# Revit family: 306_43d51a85105a496ca2926896a71aef
name_source: partatom
category: Pipe Accessories
units: mm (PartAtom-declared; Revit-internal decimal feet)

## family parameters
Always vertical = Yes
Cut with Voids When Loaded = No
Part Type = Valve - Breaks Into
Round Connector Dimension = Use Diameter
Shared = No
Work Plane-Based = No

## types (8) — shared parameters
CAT0 = Yes
Description = 3-way Control valve VLE132, PN16 external thread
L2D_Min = 3048 mm
MC = No
Manufacturer = ESBE
QmdConnectorList = 301;D;302;D
URL = http://www.esbe.eu
Z4 = 13 mm  [stored 0.0426509 ft]
Z5 = 4 mm  [stored 0.0131234 ft]
Z6 = 2 mm  [stored 0.00656168 ft]
Z7 = 15 mm  [stored 0.0492126 ft]
magiPartTypeId = 306
magiProductFamilyId = 43d51a85105a496ca2926896a71aef

## per-type parameters (varying)
- VLE132 PN16 G1 1/2 DN25-10: CenSd_D6_6=12 mm  [stored 0.0393701 ft]; D=25 mm; D1=27 mm; D13=12 mm  [stored 0.0393701 ft]; D16=19 mm  [stored 0.062336 ft]; D3=20 mm  [stored 0.0656168 ft]; D4=18 mm; D5=19 mm  [stored 0.062336 ft]; D6=14 mm  [stored 0.0459318 ft]; D7=10 mm  [stored 0.0328084 ft]; D8=5 mm  [stored 0.0164042 ft]; D9=4 mm  [stored 0.0131234 ft]; DN=20 mm  [stored 0.0656168 ft]; DN2=15 mm  [stored 0.0492126 ft]; H3=52 mm; H4=34 mm  [stored 0.111549 ft]; L2=84 mm; L2D=105 mm; LT2=53 mm; W2D=25 mm  [stored 0.082021 ft]; XN=11 mm; XN__ve=-11 mm; Z1=8 mm  [stored 0.0262467 ft]; ZR=67 mm; ZR__ve=-67 mm; magiProductId=a97d15bc2dcf492b865cbc4bb7eacc
- VLE132 PN16 G2 DN32-16: CenSd_D6_6=12 mm  [stored 0.0393701 ft]; D=32 mm; D1=27 mm; D13=12 mm  [stored 0.0393701 ft]; D16=24 mm  [stored 0.0787402 ft]; D3=20 mm  [stored 0.0656168 ft]; D4=18 mm; D5=19 mm  [stored 0.062336 ft]; D6=14 mm  [stored 0.0459318 ft]; D7=10 mm  [stored 0.0328084 ft]; D8=5 mm  [stored 0.0164042 ft]; D9=4 mm  [stored 0.0131234 ft]; DN=25 mm  [stored 0.082021 ft]; DN2=19 mm  [stored 0.062336 ft]; H3=52 mm; H4=35 mm  [stored 0.114829 ft]; L2=84 mm; L2D=105 mm; LT2=53 mm; W2D=32 mm  [stored 0.104987 ft]; XN=11 mm; XN__ve=-11 mm; Z1=8 mm  [stored 0.0262467 ft]; ZR=68 mm; ZR__ve=-68 mm; magiProductId=9854cd20be74497184f2cd1140d9ff
- VLE132 PN16 G2 3/4 DN50-38: CenSd_D6_6=17 mm  [stored 0.0557743 ft]; D=50 mm; D1=39 mm; D13=17 mm  [stored 0.0557743 ft]; D16=36 mm; D3=28 mm; D4=25 mm  [stored 0.082021 ft]; D5=27 mm; D6=20 mm  [stored 0.0656168 ft]; D7=14 mm  [stored 0.0459318 ft]; D8=7 mm  [stored 0.0229659 ft]; D9=6 mm  [stored 0.019685 ft]; DN=38 mm; DN2=28 mm; H3=75 mm; H4=53 mm; L2=120 mm; L2D=150 mm; LT2=75 mm; W2D=50 mm; XN=15 mm  [stored 0.0492126 ft]; XN__ve=-15 mm  [stored -0.0492126 ft]; Z1=12 mm  [stored 0.0393701 ft]; ZR=101 mm; ZR__ve=-101 mm  [stored -0.331365 ft]; magiProductId=2d950c02749147679a54894fce8089
- VLE132 PN16 G2 1/4 DN40-25: CenSd_D6_6=15 mm  [stored 0.0492126 ft]; D=40 mm; D1=34 mm  [stored 0.111549 ft]; D13=15 mm  [stored 0.0492126 ft]; D16=29 mm; D3=24 mm  [stored 0.0787402 ft]; D4=22 mm; D5=23 mm; D6=17 mm  [stored 0.0557743 ft]; D7=12 mm  [stored 0.0393701 ft]; D8=6 mm  [stored 0.019685 ft]; D9=5 mm  [stored 0.0164042 ft]; DN=30 mm  [stored 0.0984252 ft]; DN2=23 mm; H3=60 mm; H4=42 mm; L2=104 mm; L2D=130 mm; LT2=65 mm; W2D=40 mm; XN=13 mm  [stored 0.0426509 ft]; XN__ve=-13 mm  [stored -0.0426509 ft]; Z1=9 mm  [stored 0.0295276 ft]; ZR=80 mm; ZR__ve=-80 mm  [stored -0.262467 ft]; magiProductId=fa06140f867c4540991b35142331b7
- VLE132 PN16 G1 DN15-4,0: CenSd_D6_6=12 mm  [stored 0.0393701 ft]; D=15 mm; D1=26 mm  [stored 0.0853018 ft]; D13=11 mm; D16=12 mm  [stored 0.0393701 ft]; D3=19 mm  [stored 0.062336 ft]; D4=17 mm  [stored 0.0557743 ft]; D5=18 mm; D6=13 mm  [stored 0.0426509 ft]; D7=9 mm  [stored 0.0295276 ft]; D8=5 mm  [stored 0.0164042 ft]; D9=4 mm  [stored 0.0131234 ft]; DN=13 mm  [stored 0.0426509 ft]; DN2=9 mm  [stored 0.0295276 ft]; H3=50 mm; H4=24 mm  [stored 0.0787402 ft]; L2=80 mm; L2D=100 mm; LT2=50 mm; W2D=15 mm  [stored 0.0492126 ft]; XN=10 mm  [stored 0.0328084 ft]; XN__ve=-10 mm  [stored -0.0328084 ft]; Z1=8 mm  [stored 0.0262467 ft]; ZR=56 mm; ZR__ve=-56 mm  [stored -0.183727 ft]; magiProductId=c5e55454215b4ebea7e3226386bd84
- VLE132 PN16 G1 DN15-2,5: CenSd_D6_6=12 mm  [stored 0.0393701 ft]; D=15 mm; D1=26 mm  [stored 0.0853018 ft]; D13=11 mm; D16=12 mm  [stored 0.0393701 ft]; D3=19 mm  [stored 0.062336 ft]; D4=17 mm  [stored 0.0557743 ft]; D5=18 mm; D6=13 mm  [stored 0.0426509 ft]; D7=9 mm  [stored 0.0295276 ft]; D8=5 mm  [stored 0.0164042 ft]; D9=4 mm  [stored 0.0131234 ft]; DN=13 mm  [stored 0.0426509 ft]; DN2=9 mm  [stored 0.0295276 ft]; H3=50 mm; H4=24 mm  [stored 0.0787402 ft]; L2=80 mm; L2D=100 mm; LT2=50 mm; W2D=15 mm  [stored 0.0492126 ft]; XN=10 mm  [stored 0.0328084 ft]; XN__ve=-10 mm  [stored -0.0328084 ft]; Z1=8 mm  [stored 0.0262467 ft]; ZR=56 mm; ZR__ve=-56 mm  [stored -0.183727 ft]; magiProductId=6abd336f65614252a04a9e579203c6
- VLE132 PN16 G1 DN15-1,6: CenSd_D6_6=12 mm  [stored 0.0393701 ft]; D=15 mm; D1=26 mm  [stored 0.0853018 ft]; D13=11 mm; D16=12 mm  [stored 0.0393701 ft]; D3=19 mm  [stored 0.062336 ft]; D4=17 mm  [stored 0.0557743 ft]; D5=18 mm; D6=13 mm  [stored 0.0426509 ft]; D7=9 mm  [stored 0.0295276 ft]; D8=5 mm  [stored 0.0164042 ft]; D9=4 mm  [stored 0.0131234 ft]; DN=13 mm  [stored 0.0426509 ft]; DN2=9 mm  [stored 0.0295276 ft]; H3=50 mm; H4=24 mm  [stored 0.0787402 ft]; L2=80 mm; L2D=100 mm; LT2=50 mm; W2D=15 mm  [stored 0.0492126 ft]; XN=10 mm  [stored 0.0328084 ft]; XN__ve=-10 mm  [stored -0.0328084 ft]; Z1=8 mm  [stored 0.0262467 ft]; ZR=56 mm; ZR__ve=-56 mm  [stored -0.183727 ft]; magiProductId=d33faa5a060b46b8af20c53f047399
- VLE132 PN16 G1 1/4 DN20-6,3: CenSd_D6_6=12 mm  [stored 0.0393701 ft]; D=20 mm; D1=26 mm  [stored 0.0853018 ft]; D13=11 mm; D16=15 mm  [stored 0.0492126 ft]; D3=19 mm  [stored 0.062336 ft]; D4=17 mm  [stored 0.0557743 ft]; D5=18 mm; D6=13 mm  [stored 0.0426509 ft]; D7=9 mm  [stored 0.0295276 ft]; D8=5 mm  [stored 0.0164042 ft]; D9=4 mm  [stored 0.0131234 ft]; DN=16 mm  [stored 0.0524934 ft]; DN2=12 mm  [stored 0.0393701 ft]; H3=50 mm; H4=30 mm  [stored 0.0984252 ft]; L2=80 mm; L2D=100 mm; LT2=50 mm; W2D=20 mm  [stored 0.0656168 ft]; XN=10 mm  [stored 0.0328084 ft]; XN__ve=-10 mm  [stored -0.0328084 ft]; Z1=8 mm  [stored 0.0262467 ft]; ZR=62 mm; ZR__ve=-62 mm  [stored -0.203412 ft]; magiProductId=0de5b5ed9d004f918cc472fcdf5691

note: column(s) folded — value = type name in every type: magiProductCode

note: [stored X ft] marks values corroborated as IEEE doubles in the binary element streams (Revit-internal decimal feet)

## geometry (parser evidence)
native form markers: Sweep x1
no freeform markers — native parametric forms only
